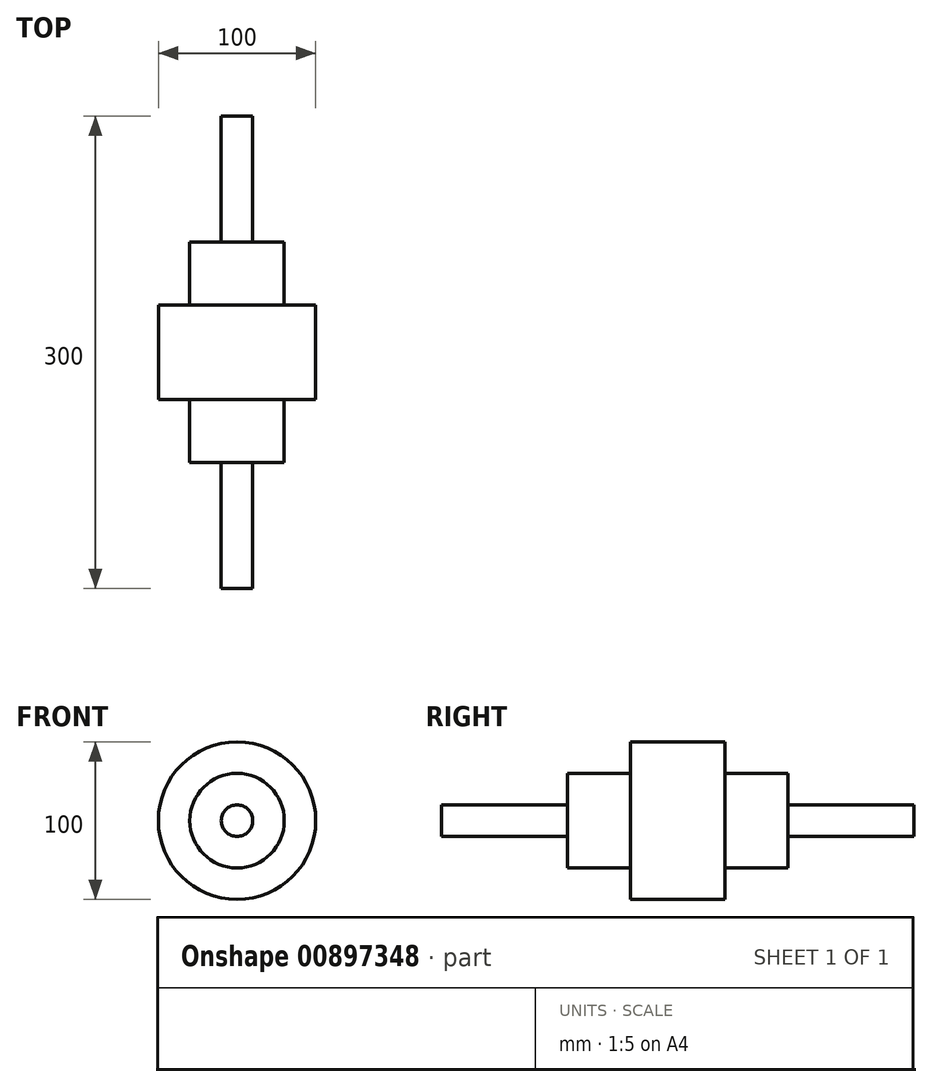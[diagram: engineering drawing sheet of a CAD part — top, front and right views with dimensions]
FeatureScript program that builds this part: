
annotation { "Feature Type Name" : "Feature", "Feature Type Description" : "" }
export const myFeature = defineFeature(function(context is Context, id is Id, definition is map)
    precondition{}
    {
        {
            var Q0;
            Q0=qCreatedBy(makeId("Front.planeOp"),FACE);
            var sketch = newSketch(context, id + "F0", { "sketchPlane" : qUnion([Q0])});
            skCircle(sketch, "E0", {"center": v(0, 0) * mm, "radius": 50 * mm});
            skSolve(sketch);
        }
        {
            var Q0;
            Q0 = qSketchRegion(id + "F0", true);
            extrude(context, id + "F1", {"entities" : qUnion([Q0]), "depth" : 60 * mm, "offsetDistance" : 25.4 * mm});
        }
        {
            var Q0;
            Q0=makeQuery(id+"F1.opExtrude","CAP_FACE",FACE,{"disambiguationData":[OSD([sQuery(id+"F0.wireOp",EDGE,"E0")])],"isStart":false});
            var sketch = newSketch(context, id + "F2", { "sketchPlane" : qUnion([Q0])});
            skCircle(sketch, "E1", {"center": v(0, 0) * mm, "radius": 30 * mm});
            skSolve(sketch);
        }
        {
            var Q0;
            Q0=makeQuery(id+"F2.imprint","IMPRINT",FACE,{"disambiguationData":[TD([[makeQuery(id+"F2.imprint","IMPRINT",EDGE,{"derivedFrom":sQuery(id+"F2.wireOp",EDGE,"E1")}),1.0]])]});
            extrude(context, id + "F3", {"entities" : qUnion([Q0]), "operationType" : NewBodyOperationType.ADD, "depth" : 40 * mm, "offsetDistance" : 25.4 * mm});
        }
        {
            var Q0;
            Q0=makeQuery(id+"F3.opExtrude","CAP_FACE",FACE,{"disambiguationData":[OSD([sQuery(id+"F2.wireOp",EDGE,"E1")])],"isStart":false});
            var sketch = newSketch(context, id + "F4", { "sketchPlane" : qUnion([Q0])});
            skCircle(sketch, "E2", {"center": v(0, 0) * mm, "radius": 10 * mm});
            skSolve(sketch);
        }
        {
            var Q0;
            Q0=makeQuery(id+"F4.imprint","IMPRINT",FACE,{"disambiguationData":[TD([[makeQuery(id+"F4.imprint","IMPRINT",EDGE,{"derivedFrom":sQuery(id+"F4.wireOp",EDGE,"E2")}),1.0]])]});
            extrude(context, id + "F5", {"entities" : qUnion([Q0]), "operationType" : NewBodyOperationType.ADD, "depth" : 80 * mm, "offsetDistance" : 25.4 * mm});
        }
        {
            var Q0;
            Q0=makeQuery(id+"F1.opExtrude","CAP_FACE",FACE,{"disambiguationData":[OSD([sQuery(id+"F0.wireOp",EDGE,"E0")])],"isStart":true});
            var sketch = newSketch(context, id + "F6", { "sketchPlane" : qUnion([Q0])});
            skCircle(sketch, "E3", {"center": v(0, 0) * mm, "radius": 30 * mm});
            skSolve(sketch);
        }
        {
            var Q0;
            Q0=makeQuery(id+"F6.imprint","IMPRINT",FACE,{"disambiguationData":[TD([[makeQuery(id+"F6.imprint","IMPRINT",EDGE,{"derivedFrom":sQuery(id+"F6.wireOp",EDGE,"E3")}),1.0]])]});
            extrude(context, id + "F7", {"entities" : qUnion([Q0]), "operationType" : NewBodyOperationType.ADD, "depth" : 40 * mm, "offsetDistance" : 25.4 * mm});
        }
        {
            var Q0;
            Q0=makeQuery(id+"F7.opExtrude","CAP_FACE",FACE,{"disambiguationData":[OSD([sQuery(id+"F6.wireOp",EDGE,"E3")])],"isStart":false});
            var sketch = newSketch(context, id + "F8", { "sketchPlane" : qUnion([Q0])});
            skCircle(sketch, "E4", {"center": v(0, 0) * mm, "radius": 10 * mm});
            skSolve(sketch);
        }
        {
            var Q0;
            Q0=makeQuery(id+"F8.imprint","IMPRINT",FACE,{"disambiguationData":[TD([[makeQuery(id+"F8.imprint","IMPRINT",EDGE,{"derivedFrom":sQuery(id+"F8.wireOp",EDGE,"E4")}),1.0]])]});
            extrude(context, id + "F9", {"entities" : qUnion([Q0]), "operationType" : NewBodyOperationType.ADD, "depth" : 80 * mm, "offsetDistance" : 25.4 * mm});
        }
    });
